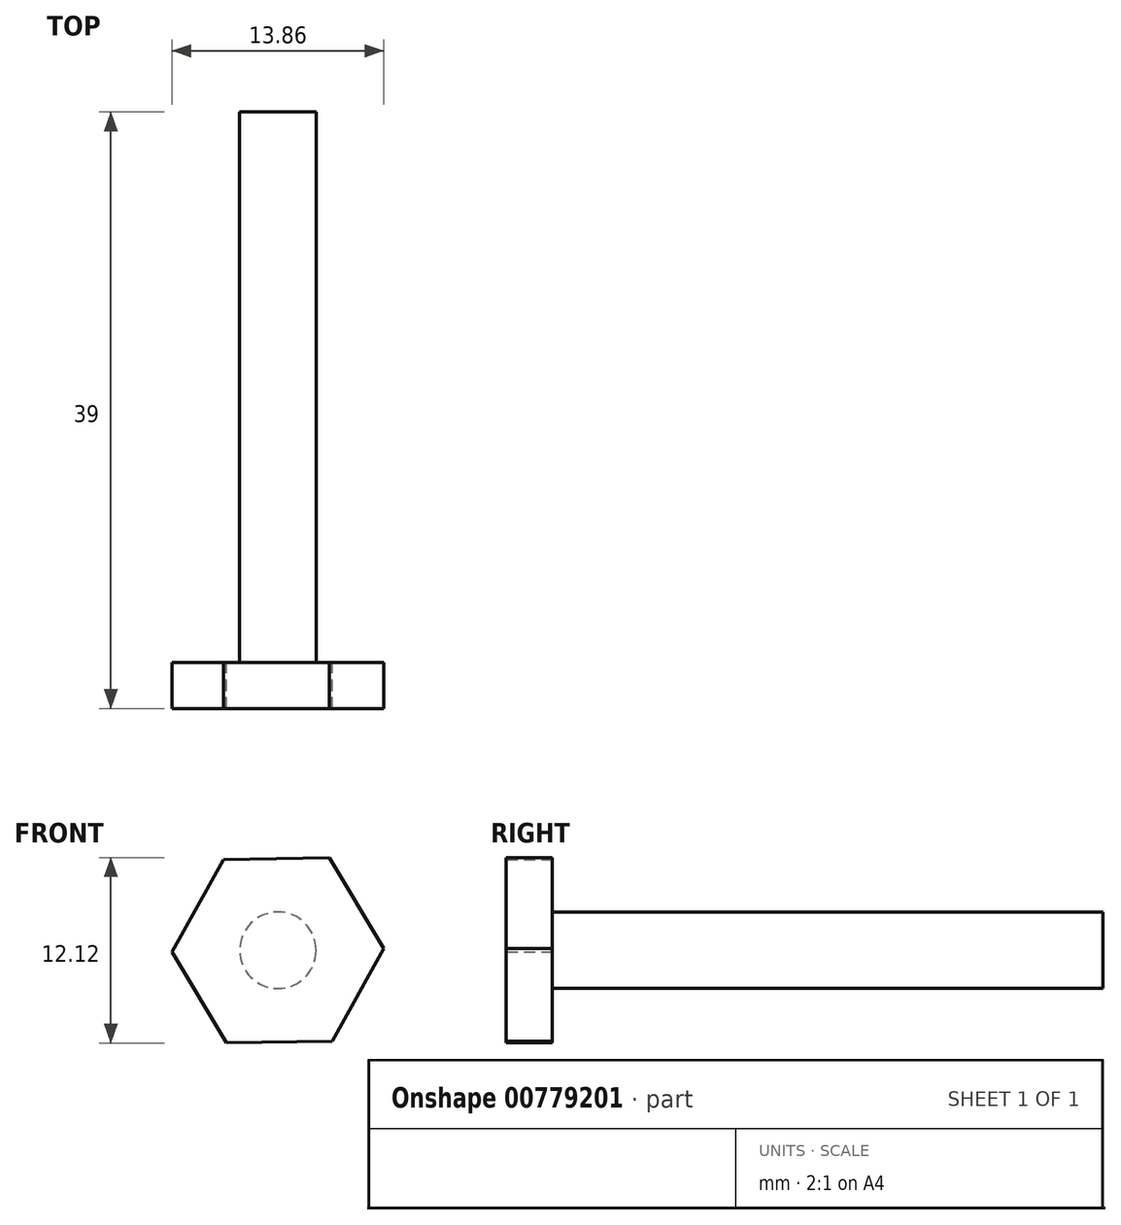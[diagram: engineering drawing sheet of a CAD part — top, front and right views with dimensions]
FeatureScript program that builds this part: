
annotation { "Feature Type Name" : "Feature", "Feature Type Description" : "" }
export const myFeature = defineFeature(function(context is Context, id is Id, definition is map)
    precondition{}
    {
        {
            var Q0;
            Q0=qCreatedBy(makeId("Front.planeOp"),FACE);
            var sketch = newSketch(context, id + "F0", { "sketchPlane" : qUnion([Q0])});
            skCircle(sketch, "E0.cCircle", {"center": v(0, 0) * mm, "radius": 6 * mm, "construction": true});
            skLineSegment(sketch, "E0.0", {"start": v(-6.93, -0.11) * mm, "end": v(-3.56, 5.94) * mm});
            skLineSegment(sketch, "E0.1", {"start": v(-3.56, 5.94) * mm, "end": v(3.36, 6.06) * mm});
            skLineSegment(sketch, "E0.2", {"start": v(3.36, 6.06) * mm, "end": v(6.93, 0.11) * mm});
            skLineSegment(sketch, "E0.3", {"start": v(6.93, 0.11) * mm, "end": v(3.56, -5.94) * mm});
            skLineSegment(sketch, "E0.4", {"start": v(3.56, -5.94) * mm, "end": v(-3.36, -6.06) * mm});
            skLineSegment(sketch, "E0.5", {"start": v(-3.36, -6.06) * mm, "end": v(-6.93, -0.11) * mm});
            skPoint(sketch, "E0.0.midPoint", {"position": v(-5.24, 2.91) * mm});
            skSolve(sketch);
        }
        {
            var Q0;
            Q0=qSketchRegion(id+"F0",true);
            extrude(context, id + "F1", {"entities" : qUnion([Q0]), "depth" : 3 * mm});
        }
        {
            var Q0;
            Q0=makeQuery(id+"F1.opExtrude","CAP_FACE",FACE,{"disambiguationData":[OSD([sQuery(id+"F0.wireOp",EDGE,"E0.0"),sQuery(id+"F0.wireOp",EDGE,"E0.1"),sQuery(id+"F0.wireOp",EDGE,"E0.2"),sQuery(id+"F0.wireOp",EDGE,"E0.3"),sQuery(id+"F0.wireOp",EDGE,"E0.4"),sQuery(id+"F0.wireOp",EDGE,"E0.5")])],"isStart":true});
            var sketch = newSketch(context, id + "F2", { "sketchPlane" : qUnion([Q0])});
            skCircle(sketch, "E1", {"center": v(0, 0) * mm, "radius": 2.5 * mm});
            skSolve(sketch);
        }
        {
            var Q0;
            Q0=qSketchRegion(id+"F2",true);
            extrude(context, id + "F3", {"entities" : qUnion([Q0]), "operationType" : NewBodyOperationType.ADD, "depth" : 36 * mm});
        }
    });
